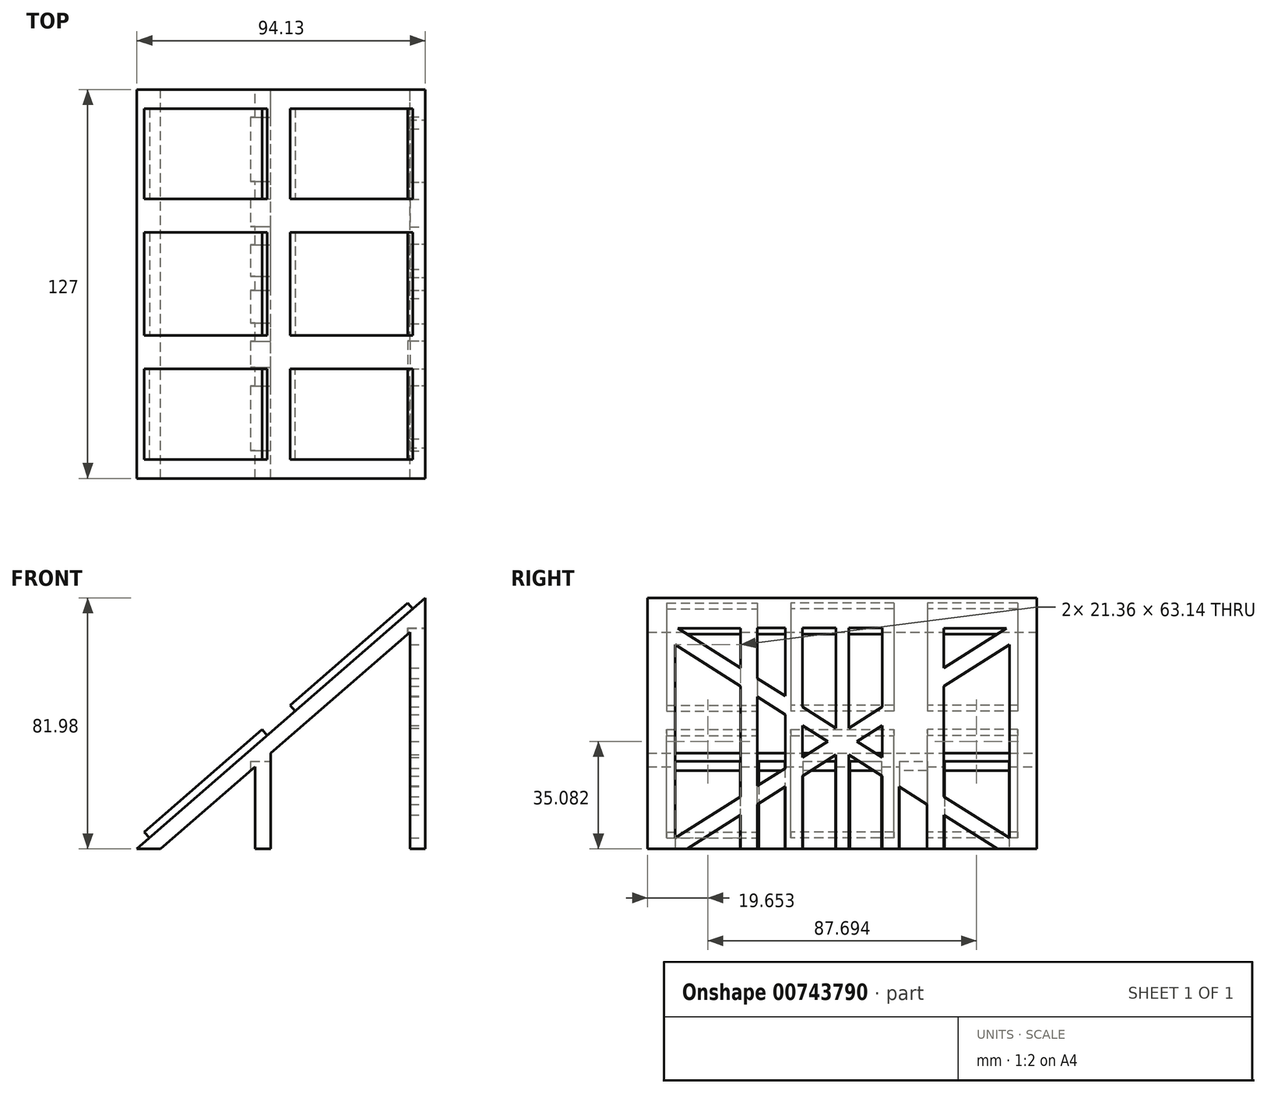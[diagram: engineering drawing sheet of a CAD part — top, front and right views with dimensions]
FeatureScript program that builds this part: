
annotation { "Feature Type Name" : "Feature", "Feature Type Description" : "" }
export const myFeature = defineFeature(function(context is Context, id is Id, definition is map)
    precondition{}
    {
        {
            var Q0;
            Q0=qCreatedBy(makeId("Front.planeOp"),FACE);
            var sketch = newSketch(context, id + "F0", { "sketchPlane" : qUnion([Q0])});
            skLineSegment(sketch, "E0", {"start": v(-47.25, 0) * mm, "end": v(-39.52, 0) * mm});
            skLineSegment(sketch, "E1", {"start": v(46.88, 0) * mm, "end": v(46.88, 81.98) * mm});
            skLineSegment(sketch, "E2", {"start": v(46.88, 81.98) * mm, "end": v(-47.25, 0) * mm});
            skLineSegment(sketch, "E3.0", {"start": v(41.8, 0) * mm, "end": v(41.8, 70.82) * mm});
            skLineSegment(sketch, "E4", {"start": v(-3.58, 31.3) * mm, "end": v(-3.58, 0) * mm});
            skLineSegment(sketch, "E5.0", {"start": v(-8.66, 26.87) * mm, "end": v(-8.66, 0) * mm});
            skLineSegment(sketch, "E6.trimOffspring", {"start": v(41.8, 70.82) * mm, "end": v(-3.58, 31.3) * mm});
            skLineSegment(sketch, "E7.trimOffspring", {"start": v(-8.66, 0) * mm, "end": v(-3.58, 0) * mm});
            skLineSegment(sketch, "E8.trimOffspring", {"start": v(41.8, 0) * mm, "end": v(46.88, 0) * mm});
            skLineSegment(sketch, "E9.trimOffspring", {"start": v(-8.66, 26.87) * mm, "end": v(-39.52, 0) * mm});
            skSolve(sketch);
        }
        {
            var Q0;
            Q0=makeQuery(id+"F0.imprint","IMPRINT",FACE,{"disambiguationData":[TD([[makeQuery(id+"F0.imprint","IMPRINT",EDGE,{"derivedFrom":sQuery(id+"F0.wireOp",EDGE,"E0")}),1.0]])]});
            extrude(context, id + "F1", {"entities" : qUnion([Q0]), "depth" : 127 * mm, "offsetDistance" : 25.4 * mm});
        }
        {
            var Q0;
            Q0=makeQuery(id+"F1.opExtrude","SWEPT_FACE",FACE,{"disambiguationData":[OSD([sQuery(id+"F0.wireOp",EDGE,"E1")])]});
            var sketch = newSketch(context, id + "F2", { "sketchPlane" : qUnion([Q0])});
            skLineSegment(sketch, "E10.bottom", {"start": v(-118.03, 0) * mm, "end": v(-96.67, 0) * mm});
            skLineSegment(sketch, "E10.top", {"start": v(-117.07, 72.06) * mm, "end": v(-96.67, 72.06) * mm});
            skLineSegment(sketch, "E10.left", {"start": v(-118.03, 3.51) * mm, "end": v(-118.03, 66.65) * mm});
            skLineSegment(sketch, "E10.right", {"start": v(-96.67, 0) * mm, "end": v(-96.67, 11.04) * mm});
            skLineSegment(sketch, "E11.bottom", {"start": v(-91.2, 72.13) * mm, "end": v(-82.07, 72.13) * mm});
            skLineSegment(sketch, "E11.top", {"start": v(-91.2, 0) * mm, "end": v(-82.07, 0) * mm});
            skLineSegment(sketch, "E11.left", {"start": v(-91.2, 72.13) * mm, "end": v(-91.2, 55.65) * mm});
            skLineSegment(sketch, "E11.right", {"start": v(-82.07, 72.13) * mm, "end": v(-82.07, 49.87) * mm});
            skLineSegment(sketch, "E12.bottom", {"start": v(-65.59, 0) * mm, "end": v(-76.53, 0) * mm});
            skLineSegment(sketch, "E12.top", {"start": v(-65.59, 72.13) * mm, "end": v(-76.53, 72.13) * mm});
            skLineSegment(sketch, "E12.left", {"start": v(-65.59, 0) * mm, "end": v(-65.59, 30.75) * mm});
            skLineSegment(sketch, "E12.right", {"start": v(-76.53, 0) * mm, "end": v(-76.53, 23.81) * mm});
            skLineSegment(sketch, "E13.MirrorCS", {"start": v(-61.41, 0) * mm, "end": v(-61.41, 30.75) * mm});
            skLineSegment(sketch, "E14.MirrorCS", {"start": v(-61.41, 72.13) * mm, "end": v(-50.47, 72.13) * mm});
            skLineSegment(sketch, "E15.MirrorCS", {"start": v(-50.47, 0) * mm, "end": v(-50.47, 23.81) * mm});
            skLineSegment(sketch, "E16.MirrorCS", {"start": v(-44.93, 72.13) * mm, "end": v(-44.93, 49.87) * mm});
            skLineSegment(sketch, "E17.MirrorCS", {"start": v(-35.8, 72.13) * mm, "end": v(-44.93, 72.13) * mm});
            skLineSegment(sketch, "E18.MirrorCS", {"start": v(-35.8, 72.13) * mm, "end": v(-35.8, 55.65) * mm});
            skLineSegment(sketch, "E19.MirrorCS", {"start": v(-30.33, 0) * mm, "end": v(-30.33, 11.04) * mm});
            skLineSegment(sketch, "E20.MirrorCS", {"start": v(-9.93, 72.06) * mm, "end": v(-30.33, 72.06) * mm});
            skLineSegment(sketch, "E21.MirrorCS", {"start": v(-8.97, 3.51) * mm, "end": v(-8.97, 66.65) * mm});
            skLineSegment(sketch, "E22", {"start": v(-117.07, 72.06) * mm, "end": v(-96.67, 59.12) * mm});
            skLineSegment(sketch, "E23.0", {"start": v(-118.03, 66.65) * mm, "end": v(-96.67, 53.1) * mm});
            skLineSegment(sketch, "E24.MirrorCS", {"start": v(-8.97, 66.65) * mm, "end": v(-30.33, 53.1) * mm});
            skLineSegment(sketch, "E25.MirrorCS", {"start": v(-9.93, 72.06) * mm, "end": v(-30.33, 59.12) * mm});
            skLineSegment(sketch, "E26.trimOffspring", {"start": v(-76.53, 46.35) * mm, "end": v(-65.59, 39.41) * mm});
            skLineSegment(sketch, "E27.trimOffspring", {"start": v(-76.53, 40.34) * mm, "end": v(-68.24, 35.08) * mm});
            skLineSegment(sketch, "E28.trimOffspring", {"start": v(-91.2, 49.63) * mm, "end": v(-82.07, 43.85) * mm});
            skLineSegment(sketch, "E29.trimOffspring", {"start": v(-91.2, 55.65) * mm, "end": v(-82.07, 49.87) * mm});
            skLineSegment(sketch, "E30.trimOffspring", {"start": v(-96.67, 17.06) * mm, "end": v(-96.67, 53.1) * mm});
            skLineSegment(sketch, "E31.trimOffspring", {"start": v(-96.67, 17.06) * mm, "end": v(-118.03, 3.51) * mm});
            skLineSegment(sketch, "E32.trimOffspring", {"start": v(-91.2, 14.51) * mm, "end": v(-91.2, 0) * mm});
            skLineSegment(sketch, "E33.trimOffspring", {"start": v(-96.67, 11.04) * mm, "end": v(-114.08, 0) * mm});
            skLineSegment(sketch, "E34.trimOffspring", {"start": v(-82.07, 43.85) * mm, "end": v(-82.07, 26.31) * mm});
            skLineSegment(sketch, "E35.trimOffspring", {"start": v(-76.53, 46.35) * mm, "end": v(-76.53, 72.13) * mm});
            skLineSegment(sketch, "E36.trimOffspring", {"start": v(-91.2, 49.63) * mm, "end": v(-91.2, 20.53) * mm});
            skLineSegment(sketch, "E37.trimOffspring", {"start": v(-96.67, 59.12) * mm, "end": v(-96.67, 72.06) * mm});
            skPoint(sketch, "E38.orphan", {"position": v(-115.3, -0.78) * mm});
            skLineSegment(sketch, "E39.trimOffspring", {"start": v(-82.07, 20.3) * mm, "end": v(-91.2, 14.51) * mm});
            skLineSegment(sketch, "E40.trimOffspring", {"start": v(-76.53, 29.83) * mm, "end": v(-76.53, 40.34) * mm});
            skLineSegment(sketch, "E41.trimOffspring", {"start": v(-82.07, 26.31) * mm, "end": v(-91.2, 20.53) * mm});
            skLineSegment(sketch, "E42.trimOffspring", {"start": v(-82.07, 20.3) * mm, "end": v(-82.07, 0) * mm});
            skPoint(sketch, "E43.orphan", {"position": v(-119.79, 67.77) * mm});
            skPoint(sketch, "E44.orphan", {"position": v(-63.5, 81.98) * mm});
            skLineSegment(sketch, "E45.trimOffspring", {"start": v(-58.76, 35.08) * mm, "end": v(-50.47, 29.83) * mm});
            skLineSegment(sketch, "E46.trimOffspring", {"start": v(-68.24, 35.08) * mm, "end": v(-76.53, 29.83) * mm});
            skLineSegment(sketch, "E47.trimOffspring", {"start": v(-61.41, 30.75) * mm, "end": v(-50.47, 23.81) * mm});
            skLineSegment(sketch, "E48.trimOffspring", {"start": v(-65.59, 30.75) * mm, "end": v(-76.53, 23.81) * mm});
            skLineSegment(sketch, "E49.trimOffspring", {"start": v(-61.41, 39.41) * mm, "end": v(-61.41, 72.13) * mm});
            skLineSegment(sketch, "E50.trimOffspring", {"start": v(-65.59, 39.41) * mm, "end": v(-65.59, 72.13) * mm});
            skPoint(sketch, "E51.end.orphan", {"position": v(-63.5, 0) * mm});
            skLineSegment(sketch, "E52.trimOffspring", {"start": v(-44.93, 43.85) * mm, "end": v(-44.93, 26.31) * mm});
            skLineSegment(sketch, "E53.trimOffspring", {"start": v(-50.47, 46.35) * mm, "end": v(-61.41, 39.41) * mm});
            skLineSegment(sketch, "E54.trimOffspring", {"start": v(-50.47, 46.35) * mm, "end": v(-50.47, 72.13) * mm});
            skLineSegment(sketch, "E55.trimOffspring", {"start": v(-50.47, 40.34) * mm, "end": v(-58.76, 35.08) * mm});
            skLineSegment(sketch, "E56.trimOffspring", {"start": v(-35.8, 55.65) * mm, "end": v(-44.93, 49.87) * mm});
            skLineSegment(sketch, "E57.trimOffspring", {"start": v(-30.33, 59.12) * mm, "end": v(-30.33, 72.06) * mm});
            skLineSegment(sketch, "E58.trimOffspring", {"start": v(-35.8, 49.63) * mm, "end": v(-44.93, 43.85) * mm});
            skLineSegment(sketch, "E59.trimOffspring", {"start": v(-35.8, 49.63) * mm, "end": v(-35.8, 20.53) * mm});
            skLineSegment(sketch, "E60.trimOffspring", {"start": v(-44.93, 20.3) * mm, "end": v(-35.8, 14.51) * mm});
            skLineSegment(sketch, "E61.trimOffspring", {"start": v(-44.93, 26.31) * mm, "end": v(-35.8, 20.53) * mm});
            skLineSegment(sketch, "E62.trimOffspring", {"start": v(-44.93, 20.3) * mm, "end": v(-44.93, 0) * mm});
            skLineSegment(sketch, "E63.trimOffspring", {"start": v(-50.47, 29.83) * mm, "end": v(-50.47, 40.34) * mm});
            skLineSegment(sketch, "E64.trimOffspring", {"start": v(-35.8, 14.51) * mm, "end": v(-35.8, 0) * mm});
            skLineSegment(sketch, "E65.trimOffspring", {"start": v(-30.33, 17.06) * mm, "end": v(-30.33, 53.1) * mm});
            skLineSegment(sketch, "E66.trimOffspring", {"start": v(-30.33, 11.04) * mm, "end": v(-12.92, 0) * mm});
            skLineSegment(sketch, "E67.trimOffspring", {"start": v(-30.33, 17.06) * mm, "end": v(-8.97, 3.51) * mm});
            skPoint(sketch, "E68.end.orphan", {"position": v(-11.2, 0) * mm});
            skPoint(sketch, "E69.orphan", {"position": v(-8.97, 0) * mm});
            skLineSegment(sketch, "E70", {"start": v(-30.33, 0) * mm, "end": v(-8.97, 0) * mm});
            skSolve(sketch);
        }
        {
            var Q0;
            Q0=makeQuery(id+"F2.imprint","IMPRINT",FACE,{"disambiguationData":[TD([[makeQuery(id+"F2.imprint","IMPRINT",EDGE,{"derivedFrom":sQuery(id+"F2.wireOp",EDGE,"E45.trimOffspring")}),1.0]])]});
            var Q1;
            Q1=makeQuery(id+"F2.imprint","IMPRINT",FACE,{"disambiguationData":[TD([[makeQuery(id+"F2.imprint","IMPRINT",EDGE,{"derivedFrom":sQuery(id+"F2.wireOp",EDGE,"E52.trimOffspring")}),1.0]])]});
            var Q2;
            Q2=makeQuery(id+"F2.imprint","IMPRINT",FACE,{"disambiguationData":[TD([[makeQuery(id+"F2.imprint","IMPRINT",EDGE,{"derivedFrom":sQuery(id+"F2.wireOp",EDGE,"E21.MirrorCS")}),1.0]])]});
            var Q3;
            {var subQ0=sQuery(id+"F2.wireOp",EDGE,"E19.MirrorCS");Q3=makeQuery(id+"F2.imprint","IMPRINT",FACE,{"disambiguationData":[TD([[makeQuery(id+"F2.imprint","IMPRINT",EDGE,{"derivedFrom":subQ0}),-1.0]])]});}
            var Q4;
            Q4=makeQuery(id+"F2.imprint","IMPRINT",FACE,{"disambiguationData":[TD([[makeQuery(id+"F2.imprint","IMPRINT",EDGE,{"derivedFrom":sQuery(id+"F2.wireOp",EDGE,"E60.trimOffspring")}),-1.0]])]});
            var Q5;
            {var subQ0=sQuery(id+"F2.wireOp",EDGE,"E13.MirrorCS");Q5=makeQuery(id+"F2.imprint","IMPRINT",FACE,{"disambiguationData":[TD([[makeQuery(id+"F2.imprint","IMPRINT",EDGE,{"derivedFrom":subQ0}),-1.0]])]});}
            var Q6;
            Q6=makeQuery(id+"F2.imprint","IMPRINT",FACE,{"disambiguationData":[TD([[makeQuery(id+"F2.imprint","IMPRINT",EDGE,{"derivedFrom":sQuery(id+"F2.wireOp",EDGE,"E12.bottom")}),1.0]])]});
            var Q7;
            Q7=makeQuery(id+"F2.imprint","IMPRINT",FACE,{"disambiguationData":[TD([[makeQuery(id+"F2.imprint","IMPRINT",EDGE,{"derivedFrom":sQuery(id+"F2.wireOp",EDGE,"E11.top")}),1.0]])]});
            var Q8;
            {var subQ0=sQuery(id+"F2.wireOp",EDGE,"E10.right");Q8=makeQuery(id+"F2.imprint","IMPRINT",FACE,{"disambiguationData":[TD([[makeQuery(id+"F2.imprint","IMPRINT",EDGE,{"derivedFrom":subQ0}),1.0]])]});}
            var Q9;
            Q9=makeQuery(id+"F2.imprint","IMPRINT",FACE,{"disambiguationData":[TD([[makeQuery(id+"F2.imprint","IMPRINT",EDGE,{"derivedFrom":sQuery(id+"F2.wireOp",EDGE,"E10.left")}),-1.0]])]});
            var Q10;
            Q10=makeQuery(id+"F2.imprint","IMPRINT",FACE,{"disambiguationData":[TD([[makeQuery(id+"F2.imprint","IMPRINT",EDGE,{"derivedFrom":sQuery(id+"F2.wireOp",EDGE,"E28.trimOffspring")}),-1.0]])]});
            var Q11;
            Q11=makeQuery(id+"F2.imprint","IMPRINT",FACE,{"disambiguationData":[TD([[makeQuery(id+"F2.imprint","IMPRINT",EDGE,{"derivedFrom":sQuery(id+"F2.wireOp",EDGE,"E27.trimOffspring")}),-1.0]])]});
            var Q12;
            Q12=makeQuery(id+"F2.imprint","IMPRINT",FACE,{"disambiguationData":[TD([[makeQuery(id+"F2.imprint","IMPRINT",EDGE,{"derivedFrom":sQuery(id+"F2.wireOp",EDGE,"E12.top")}),1.0]])]});
            var Q13;
            Q13=makeQuery(id+"F2.imprint","IMPRINT",FACE,{"disambiguationData":[TD([[makeQuery(id+"F2.imprint","IMPRINT",EDGE,{"derivedFrom":sQuery(id+"F2.wireOp",EDGE,"E10.top")}),-1.0]])]});
            var Q14;
            Q14=makeQuery(id+"F2.imprint","IMPRINT",FACE,{"disambiguationData":[TD([[makeQuery(id+"F2.imprint","IMPRINT",EDGE,{"derivedFrom":sQuery(id+"F2.wireOp",EDGE,"E11.bottom")}),-1.0]])]});
            var Q15;
            Q15=makeQuery(id+"F2.imprint","IMPRINT",FACE,{"disambiguationData":[TD([[makeQuery(id+"F2.imprint","IMPRINT",EDGE,{"derivedFrom":sQuery(id+"F2.wireOp",EDGE,"E14.MirrorCS")}),-1.0]])]});
            var Q16;
            Q16=makeQuery(id+"F2.imprint","IMPRINT",FACE,{"disambiguationData":[TD([[makeQuery(id+"F2.imprint","IMPRINT",EDGE,{"derivedFrom":sQuery(id+"F2.wireOp",EDGE,"E16.MirrorCS")}),1.0]])]});
            var Q17;
            Q17=makeQuery(id+"F2.imprint","IMPRINT",FACE,{"disambiguationData":[TD([[makeQuery(id+"F2.imprint","IMPRINT",EDGE,{"derivedFrom":sQuery(id+"F2.wireOp",EDGE,"E20.MirrorCS")}),1.0]])]});
            extrude(context, id + "F3", {"entities" : qUnion([Q0, Q1, Q2, Q3, Q4, Q5, Q6, Q7, Q8, Q9, Q10, Q11, Q12, Q13, Q14, Q15, Q16, Q17]), "operationType" : NewBodyOperationType.REMOVE, "oppositeDirection" : true, "depth" : 5.84 * mm, "offsetDistance" : 25.4 * mm});
        }
        {
            var Q0;
            Q0=makeQuery(id+"F1.opExtrude","SWEPT_FACE",FACE,{"disambiguationData":[OSD([sQuery(id+"F0.wireOp",EDGE,"E4")])]});
            var sketch = newSketch(context, id + "F4", { "sketchPlane" : qUnion([Q0])});
            skSolve(sketch);
        }
        {
            var Q0;
            {var subQ0=sQuery(id+"F0.wireOp",EDGE,"E4");Q0=makeQuery(id+"F4.imprint","IMPRINT",FACE,{"disambiguationData":[TD([[makeQuery(id+"F4.imprint","IMPRINT",EDGE,{"derivedFrom":makeQuery(id+"F1.opExtrude","CAP_EDGE",EDGE,{"disambiguationData":[OSD([subQ0])],"isStart":true})}),-1.0]])]});}
            var sketch = newSketch(context, id + "F5", { "sketchPlane" : qUnion([Q0])});
            skLineSegment(sketch, "E71.bottom", {"start": v(-117.97, 28.62) * mm, "end": v(-96.8, 28.62) * mm});
            skLineSegment(sketch, "E71.top", {"start": v(-117.97, 0) * mm, "end": v(-96.8, 0) * mm});
            skLineSegment(sketch, "E71.left", {"start": v(-117.97, 28.62) * mm, "end": v(-117.97, 0) * mm});
            skLineSegment(sketch, "E71.right", {"start": v(-96.8, 28.62) * mm, "end": v(-96.8, 0) * mm});
            skLineSegment(sketch, "E72.bottom", {"start": v(-90.7, 28.62) * mm, "end": v(-82.22, 28.62) * mm});
            skLineSegment(sketch, "E72.top", {"start": v(-90.7, 0) * mm, "end": v(-82.22, 0) * mm});
            skLineSegment(sketch, "E72.left", {"start": v(-90.7, 28.62) * mm, "end": v(-90.7, 0) * mm});
            skLineSegment(sketch, "E72.right", {"start": v(-82.22, 28.62) * mm, "end": v(-82.22, 0) * mm});
            skLineSegment(sketch, "E73.bottom", {"start": v(-76.31, 28.62) * mm, "end": v(-65.63, 28.62) * mm});
            skLineSegment(sketch, "E73.top", {"start": v(-76.31, -2.13) * mm, "end": v(-65.63, -2.13) * mm});
            skLineSegment(sketch, "E73.left", {"start": v(-76.31, 28.62) * mm, "end": v(-76.31, -2.13) * mm});
            skLineSegment(sketch, "E73.right", {"start": v(-65.63, 28.62) * mm, "end": v(-65.63, -2.13) * mm});
            skLineSegment(sketch, "E74.bottom", {"start": v(-60.96, 28.62) * mm, "end": v(-50.67, 28.62) * mm});
            skLineSegment(sketch, "E74.top", {"start": v(-60.96, -2.13) * mm, "end": v(-50.67, -2.13) * mm});
            skLineSegment(sketch, "E74.left", {"start": v(-60.96, 28.62) * mm, "end": v(-60.96, -2.13) * mm});
            skLineSegment(sketch, "E74.right", {"start": v(-50.67, 28.62) * mm, "end": v(-50.67, -2.13) * mm});
            skLineSegment(sketch, "E75.bottom", {"start": v(-44.82, 28.62) * mm, "end": v(-35.75, 28.62) * mm});
            skLineSegment(sketch, "E75.top", {"start": v(-44.82, 0) * mm, "end": v(-35.75, 0) * mm});
            skLineSegment(sketch, "E75.left", {"start": v(-44.82, 28.62) * mm, "end": v(-44.82, 0) * mm});
            skLineSegment(sketch, "E75.right", {"start": v(-35.75, 28.62) * mm, "end": v(-35.75, 0) * mm});
            skLineSegment(sketch, "E76.bottom", {"start": v(-30.08, 28.62) * mm, "end": v(-9.1, 28.62) * mm});
            skLineSegment(sketch, "E76.top", {"start": v(-30.08, 0) * mm, "end": v(-9.1, 0) * mm});
            skLineSegment(sketch, "E76.left", {"start": v(-30.08, 28.62) * mm, "end": v(-30.08, 0) * mm});
            skLineSegment(sketch, "E76.right", {"start": v(-9.1, 28.62) * mm, "end": v(-9.1, 0) * mm});
            skSolve(sketch);
        }
        {
            var Q0;
            Q0=makeQuery(id+"F5.imprint","IMPRINT",FACE,{"disambiguationData":[TD([[makeQuery(id+"F5.imprint","IMPRINT",EDGE,{"derivedFrom":sQuery(id+"F5.wireOp",EDGE,"E71.bottom")}),-1.0]])]});
            var Q1;
            Q1=makeQuery(id+"F5.imprint","IMPRINT",FACE,{"disambiguationData":[TD([[makeQuery(id+"F5.imprint","IMPRINT",EDGE,{"derivedFrom":sQuery(id+"F5.wireOp",EDGE,"E72.bottom")}),-1.0]])]});
            var Q2;
            {var subQ0=sQuery(id+"F5.wireOp",EDGE,"E73.bottom");Q2=makeQuery(id+"F5.imprint","IMPRINT",FACE,{"disambiguationData":[TD([[makeQuery(id+"F5.imprint","IMPRINT",EDGE,{"derivedFrom":subQ0}),-1.0]])]});}
            var Q3;
            {var subQ0=sQuery(id+"F5.wireOp",EDGE,"E74.bottom");Q3=makeQuery(id+"F5.imprint","IMPRINT",FACE,{"disambiguationData":[TD([[makeQuery(id+"F5.imprint","IMPRINT",EDGE,{"derivedFrom":subQ0}),-1.0]])]});}
            var Q4;
            Q4=makeQuery(id+"F5.imprint","IMPRINT",FACE,{"disambiguationData":[TD([[makeQuery(id+"F5.imprint","IMPRINT",EDGE,{"derivedFrom":sQuery(id+"F5.wireOp",EDGE,"E75.bottom")}),-1.0]])]});
            var Q5;
            Q5=makeQuery(id+"F5.imprint","IMPRINT",FACE,{"disambiguationData":[TD([[makeQuery(id+"F5.imprint","IMPRINT",EDGE,{"derivedFrom":sQuery(id+"F5.wireOp",EDGE,"E76.bottom")}),-1.0]])]});
            extrude(context, id + "F6", {"entities" : qUnion([Q0, Q1, Q2, Q3, Q4, Q5]), "operationType" : NewBodyOperationType.REMOVE, "oppositeDirection" : true, "depth" : 6.6 * mm, "offsetDistance" : 25.4 * mm});
        }
        {
            var Q0;
            Q0=makeQuery(id+"F1.opExtrude","SWEPT_FACE",FACE,{"disambiguationData":[OSD([sQuery(id+"F0.wireOp",EDGE,"E2")])]});
            var sketch = newSketch(context, id + "F7", { "sketchPlane" : qUnion([Q0])});
            skLineSegment(sketch, "E77", {"start": v(-30.2, -63.5) * mm, "end": v(-35.63, -63.5) * mm});
            skLineSegment(sketch, "E78.bottom", {"start": v(83.76, -6.23) * mm, "end": v(32.8, -6.23) * mm});
            skLineSegment(sketch, "E78.top", {"start": v(83.76, -35.72) * mm, "end": v(32.8, -35.72) * mm});
            skLineSegment(sketch, "E78.left", {"start": v(83.76, -6.23) * mm, "end": v(83.76, -35.72) * mm});
            skLineSegment(sketch, "E78.right", {"start": v(32.8, -6.23) * mm, "end": v(32.8, -35.72) * mm});
            skLineSegment(sketch, "E79.bottom", {"start": v(83.76, -46.66) * mm, "end": v(32.8, -46.66) * mm});
            skLineSegment(sketch, "E79.left", {"start": v(83.76, -46.66) * mm, "end": v(83.76, -63.5) * mm});
            skLineSegment(sketch, "E79.right", {"start": v(32.8, -46.66) * mm, "end": v(32.8, -63.5) * mm});
            skLineSegment(sketch, "E80.MirrorCS", {"start": v(20.75, -6.23) * mm, "end": v(20.75, -35.72) * mm});
            skLineSegment(sketch, "E81.MirrorCS", {"start": v(20.75, -46.66) * mm, "end": v(20.75, -63.5) * mm});
            skLineSegment(sketch, "E82.MirrorCS", {"start": v(-30.2, -46.66) * mm, "end": v(20.75, -46.66) * mm});
            skLineSegment(sketch, "E83.MirrorCS", {"start": v(-30.2, -35.72) * mm, "end": v(20.75, -35.72) * mm});
            skLineSegment(sketch, "E84.MirrorCS", {"start": v(-30.2, -6.23) * mm, "end": v(-30.2, -35.72) * mm});
            skLineSegment(sketch, "E85.MirrorCS", {"start": v(-30.2, -6.23) * mm, "end": v(20.75, -6.23) * mm});
            skLineSegment(sketch, "E86.MirrorCS", {"start": v(-30.2, -46.66) * mm, "end": v(-30.2, -63.5) * mm});
            skLineSegment(sketch, "E87.MirrorCS", {"start": v(83.76, -80.34) * mm, "end": v(32.8, -80.34) * mm});
            skLineSegment(sketch, "E88.MirrorCS", {"start": v(83.76, -80.34) * mm, "end": v(83.76, -63.5) * mm});
            skLineSegment(sketch, "E89.MirrorCS", {"start": v(32.8, -80.34) * mm, "end": v(32.8, -63.5) * mm});
            skLineSegment(sketch, "E90.MirrorCS", {"start": v(83.76, -91.28) * mm, "end": v(32.8, -91.28) * mm});
            skLineSegment(sketch, "E91.MirrorCS", {"start": v(32.8, -120.77) * mm, "end": v(32.8, -91.28) * mm});
            skLineSegment(sketch, "E92.MirrorCS", {"start": v(83.76, -120.77) * mm, "end": v(32.8, -120.77) * mm});
            skLineSegment(sketch, "E93.MirrorCS", {"start": v(83.76, -120.77) * mm, "end": v(83.76, -91.28) * mm});
            skLineSegment(sketch, "E94.MirrorCS", {"start": v(-30.2, -91.28) * mm, "end": v(20.75, -91.28) * mm});
            skLineSegment(sketch, "E95.MirrorCS", {"start": v(20.75, -120.77) * mm, "end": v(20.75, -91.28) * mm});
            skLineSegment(sketch, "E96.MirrorCS", {"start": v(-30.2, -120.77) * mm, "end": v(20.75, -120.77) * mm});
            skLineSegment(sketch, "E97.MirrorCS", {"start": v(-30.2, -120.77) * mm, "end": v(-30.2, -91.28) * mm});
            skLineSegment(sketch, "E98.MirrorCS", {"start": v(-30.2, -80.34) * mm, "end": v(20.75, -80.34) * mm});
            skLineSegment(sketch, "E99.MirrorCS", {"start": v(-30.2, -80.34) * mm, "end": v(-30.2, -63.5) * mm});
            skLineSegment(sketch, "E100.MirrorCS", {"start": v(20.75, -80.34) * mm, "end": v(20.75, -63.5) * mm});
            skPoint(sketch, "E101.orphan", {"position": v(89.19, -63.5) * mm});
            skPoint(sketch, "E102.orphan", {"position": v(26.78, 0) * mm});
            skPoint(sketch, "E103.end.orphan", {"position": v(26.78, -127) * mm});
            skSolve(sketch);
        }
        {
            var Q0;
            Q0=makeQuery(id+"F7.imprint","IMPRINT",FACE,{"disambiguationData":[TD([[makeQuery(id+"F7.imprint","IMPRINT",EDGE,{"derivedFrom":sQuery(id+"F7.wireOp",EDGE,"E78.bottom")}),1.0]])]});
            var Q1;
            Q1=makeQuery(id+"F7.imprint","IMPRINT",FACE,{"disambiguationData":[TD([[makeQuery(id+"F7.imprint","IMPRINT",EDGE,{"derivedFrom":sQuery(id+"F7.wireOp",EDGE,"E79.bottom")}),1.0]])]});
            var Q2;
            Q2=makeQuery(id+"F7.imprint","IMPRINT",FACE,{"disambiguationData":[TD([[makeQuery(id+"F7.imprint","IMPRINT",EDGE,{"derivedFrom":sQuery(id+"F7.wireOp",EDGE,"E90.MirrorCS")}),1.0]])]});
            var Q3;
            Q3=makeQuery(id+"F7.imprint","IMPRINT",FACE,{"disambiguationData":[TD([[makeQuery(id+"F7.imprint","IMPRINT",EDGE,{"derivedFrom":sQuery(id+"F7.wireOp",EDGE,"E94.MirrorCS")}),-1.0]])]});
            var Q4;
            Q4=makeQuery(id+"F7.imprint","IMPRINT",FACE,{"disambiguationData":[TD([[makeQuery(id+"F7.imprint","IMPRINT",EDGE,{"derivedFrom":sQuery(id+"F7.wireOp",EDGE,"E81.MirrorCS")}),-1.0]])]});
            var Q5;
            Q5=makeQuery(id+"F7.imprint","IMPRINT",FACE,{"disambiguationData":[TD([[makeQuery(id+"F7.imprint","IMPRINT",EDGE,{"derivedFrom":sQuery(id+"F7.wireOp",EDGE,"E80.MirrorCS")}),-1.0]])]});
            extrude(context, id + "F8", {"entities" : qUnion([Q0, Q1, Q2, Q3, Q4, Q5]), "operationType" : NewBodyOperationType.ADD, "depth" : 2.54 * mm, "offsetDistance" : 25.4 * mm});
        }
    });
